# Revit family: Haworth_Lively_Chair_Side_EU_PRELIMINARY
name_source: partatom
category: Furniture
units: mm (PartAtom-declared; Revit-internal decimal feet)

## family parameters
Always vertical = Yes
Cut with Voids When Loaded = No
OmniClass Number = 23.40.70.14.64.11
OmniClass Title = Office Furniture
Room Calculation Point = No
Shared = No
Work Plane-Based = No

## types (6) — shared parameters
Assembly Code = E2020200
Back Frame Finish = Haworth _ Polymer _ Black
Depth = 59 cm
Description = Haworth - Lively - Chair - Visitor - Side
Manufacturer = Haworth
Model = 29X0
Product URL = https://www.haworth.com
Revision Number = 1
Size = Verify Final Dim. w/ Haworth
Trim Finish = Haworth _ Polymer _ Black
URL = https://www.haworth.com
Warranty = http://www.haworth.com
Width = 56 cm

## per-type parameters (varying)
| type | Arm Cap | Base Casters Armless | Base Casters Arms | Base Glides Armless | Base Glides Arms | Casters | Four Legs | Glides | Sled Base | With Arms | Without Arms |
| With Arms - Glides | Yes | No | No | No | Yes | No | Yes | Yes | No | Yes | No |
| With Arms - Casters | Yes | No | Yes | No | No | Yes | Yes | No | No | Yes | No |
| Without Arms - Glides | No | No | No | Yes | No | No | Yes | Yes | No | No | Yes |
| Without Arms - Casters | No | Yes | No | No | No | Yes | Yes | No | No | No | Yes |
| With Arms - Sled Base | No | No | No | No | No | No | No | No | Yes | Yes | No |
| Without Arms - Sled Base | No | No | No | No | No | No | No | No | Yes | No | Yes |

## geometry (parser evidence)
native form markers: Blend x12, Sweep x10
no freeform markers — native parametric forms only
